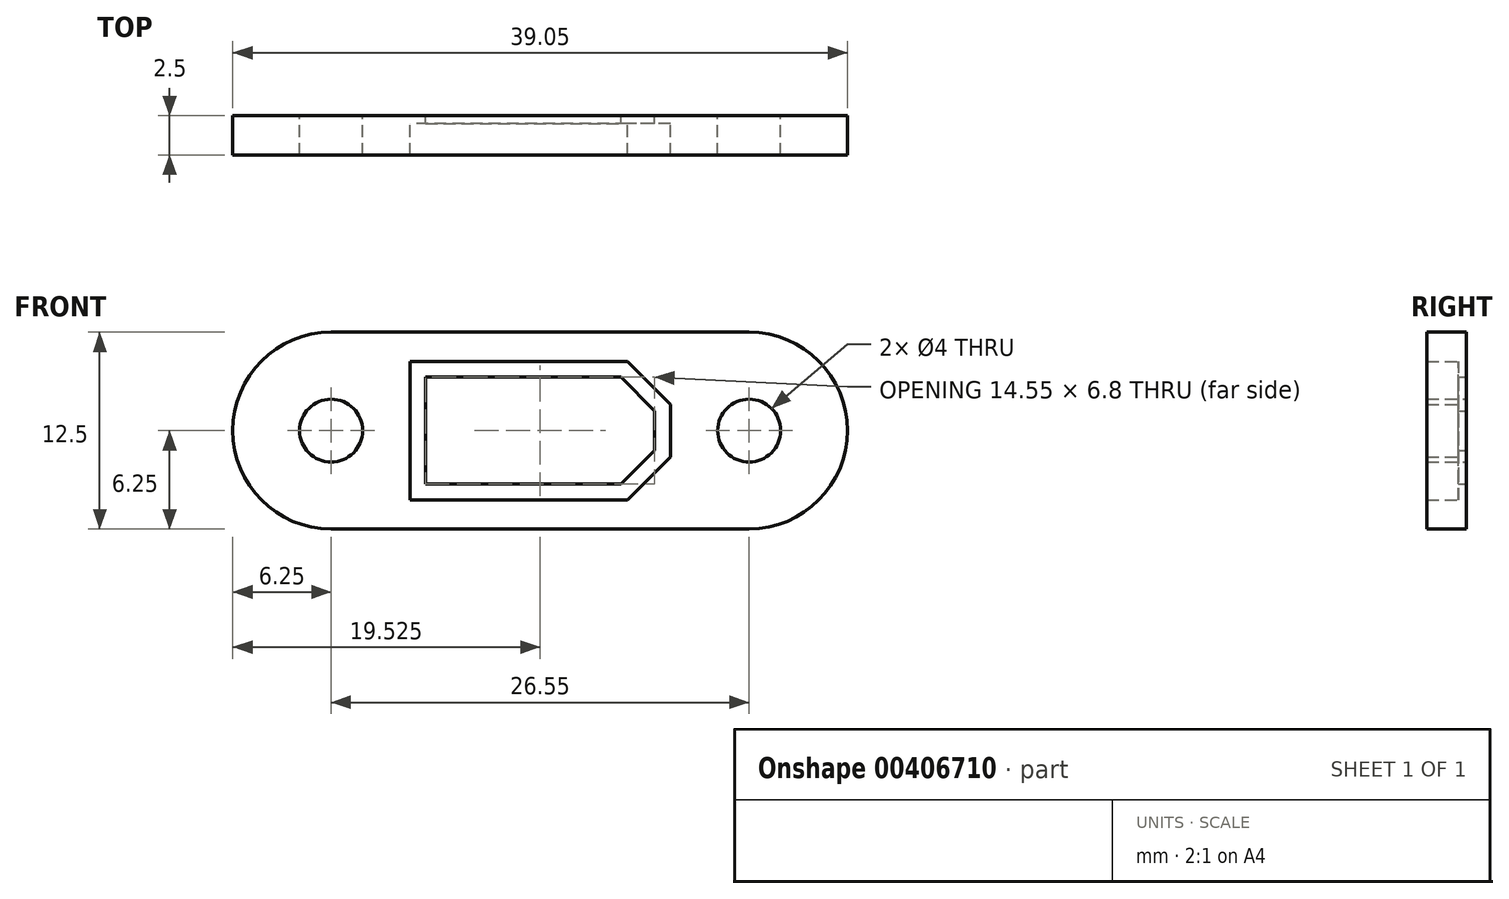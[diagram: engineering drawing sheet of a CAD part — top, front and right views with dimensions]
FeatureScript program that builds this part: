
annotation { "Feature Type Name" : "Feature", "Feature Type Description" : "" }
export const myFeature = defineFeature(function(context is Context, id is Id, definition is map)
    precondition{}
    {
        {
            var Q0;
            Q0=qCreatedBy(makeId("Front.planeOp"),FACE);
            var sketch = newSketch(context, id + "F0", { "sketchPlane" : qUnion([Q0])});
            skLineSegment(sketch, "E0", {"start": v(0, 0) * mm, "end": v(12.4, 0) * mm});
            skLineSegment(sketch, "E1", {"start": v(12.4, 0) * mm, "end": v(14.55, 2.15) * mm});
            skLineSegment(sketch, "E2", {"start": v(14.55, 2.15) * mm, "end": v(14.55, 4.65) * mm});
            skLineSegment(sketch, "E3", {"start": v(14.55, 4.65) * mm, "end": v(12.4, 6.8) * mm});
            skLineSegment(sketch, "E4", {"start": v(12.4, 6.8) * mm, "end": v(0, 6.8) * mm});
            skLineSegment(sketch, "E5", {"start": v(0, 6.8) * mm, "end": v(0, 0) * mm});
            skLineSegment(sketch, "E6.bottom", {"start": v(-6, 9.65) * mm, "end": v(20.55, 9.65) * mm});
            skLineSegment(sketch, "E6.top", {"start": v(-6, -2.85) * mm, "end": v(20.55, -2.85) * mm});
            skCircle(sketch, "E7", {"center": v(-6, 3.4) * mm, "radius": 2 * mm});
            skCircle(sketch, "E8", {"center": v(20.55, 3.4) * mm, "radius": 2 * mm});
            skArc(sketch, "E9", {"start": v(-6, 9.65) * mm, "mid": v(-12.25, 3.4) * mm, "end": v(-6, -2.85) * mm});
            skArc(sketch, "E10", {"start": v(20.55, -2.85) * mm, "mid": v(26.8, 3.4) * mm, "end": v(20.55, 9.65) * mm});
            skSolve(sketch);
        }
        {
            var Q0;
            Q0=makeQuery(id+"F0.imprint","IMPRINT",FACE,{"disambiguationData":[TD([[makeQuery(id+"F0.imprint","IMPRINT",EDGE,{"derivedFrom":sQuery(id+"F0.wireOp",EDGE,"E0")}),-1.0]])]});
            extrude(context, id + "F1", {"entities" : qUnion([Q0]), "depth" : 0.5 * mm});
        }
        {
            var Q0;
            Q0=makeQuery(id+"F1.opExtrude","CAP_FACE",FACE,{"disambiguationData":[OSD([sQuery(id+"F0.wireOp",EDGE,"E0"),sQuery(id+"F0.wireOp",EDGE,"E1"),sQuery(id+"F0.wireOp",EDGE,"E2"),sQuery(id+"F0.wireOp",EDGE,"E3"),sQuery(id+"F0.wireOp",EDGE,"E4"),sQuery(id+"F0.wireOp",EDGE,"E5"),sQuery(id+"F0.wireOp",EDGE,"E6.bottom"),sQuery(id+"F0.wireOp",EDGE,"E6.top"),sQuery(id+"F0.wireOp",EDGE,"E7"),sQuery(id+"F0.wireOp",EDGE,"E8"),sQuery(id+"F0.wireOp",EDGE,"E9"),sQuery(id+"F0.wireOp",EDGE,"E10"),sQuery(id+"F0.wireOp",EDGE,"AXl8qdVJ-KR5t-XcRl-LZmK-YnWJbsie0Hio"),sQuery(id+"F0.wireOp",EDGE,"Eh2CkkHX-vQ4I-H8gJ-Dif0-WQijSlJQoAk3"),sQuery(id+"F0.wireOp",EDGE,"r0hDG3Qd-PL5h-vyEx-fuO1-ODK39DrsAifT"),sQuery(id+"F0.wireOp",EDGE,"qWRzF2aY-tAvQ-lMVc-8J2r-1OIN6b2LeU18"),sQuery(id+"F0.wireOp",EDGE,"cb5d10df-9c84-435f-99ff-217974d2033b.filletArc"),sQuery(id+"F0.wireOp",EDGE,"c88bd7bf-c8b4-42cc-8109-43e5e4a5020a.filletArc"),sQuery(id+"F0.wireOp",EDGE,"afc00591-e2e6-4979-852d-5ef665f82a0c.filletArc"),sQuery(id+"F0.wireOp",EDGE,"6a6500f9-e719-42f7-9d80-b575ed9027c1.filletArc")])],"isStart":false});
            var sketch = newSketch(context, id + "F2", { "sketchPlane" : qUnion([Q0])});
            skLineSegment(sketch, "E11.0", {"start": v(15.55, 5.06) * mm, "end": v(12.81, 7.8) * mm});
            skLineSegment(sketch, "E11.1", {"start": v(-1, 7.8) * mm, "end": v(-1, -1) * mm});
            skLineSegment(sketch, "E11.2", {"start": v(-1, -1) * mm, "end": v(12.81, -1) * mm});
            skLineSegment(sketch, "E11.3", {"start": v(12.81, 7.8) * mm, "end": v(-1, 7.8) * mm});
            skLineSegment(sketch, "E11.4", {"start": v(12.81, -1) * mm, "end": v(15.55, 1.74) * mm});
            skLineSegment(sketch, "E11.5", {"start": v(15.55, 1.74) * mm, "end": v(15.55, 5.06) * mm});
            skSolve(sketch);
        }
        {
            var Q0;
            Q0=makeQuery(id+"F2.imprint","IMPRINT",FACE,{"disambiguationData":[TD([[makeQuery(id+"F2.imprint","IMPRINT",EDGE,{"derivedFrom":sQuery(id+"F2.wireOp",EDGE,"E11.0")}),-1.0]])]});
            extrude(context, id + "F3", {"entities" : qUnion([Q0]), "operationType" : NewBodyOperationType.ADD, "depth" : 2 * mm});
        }
    });
